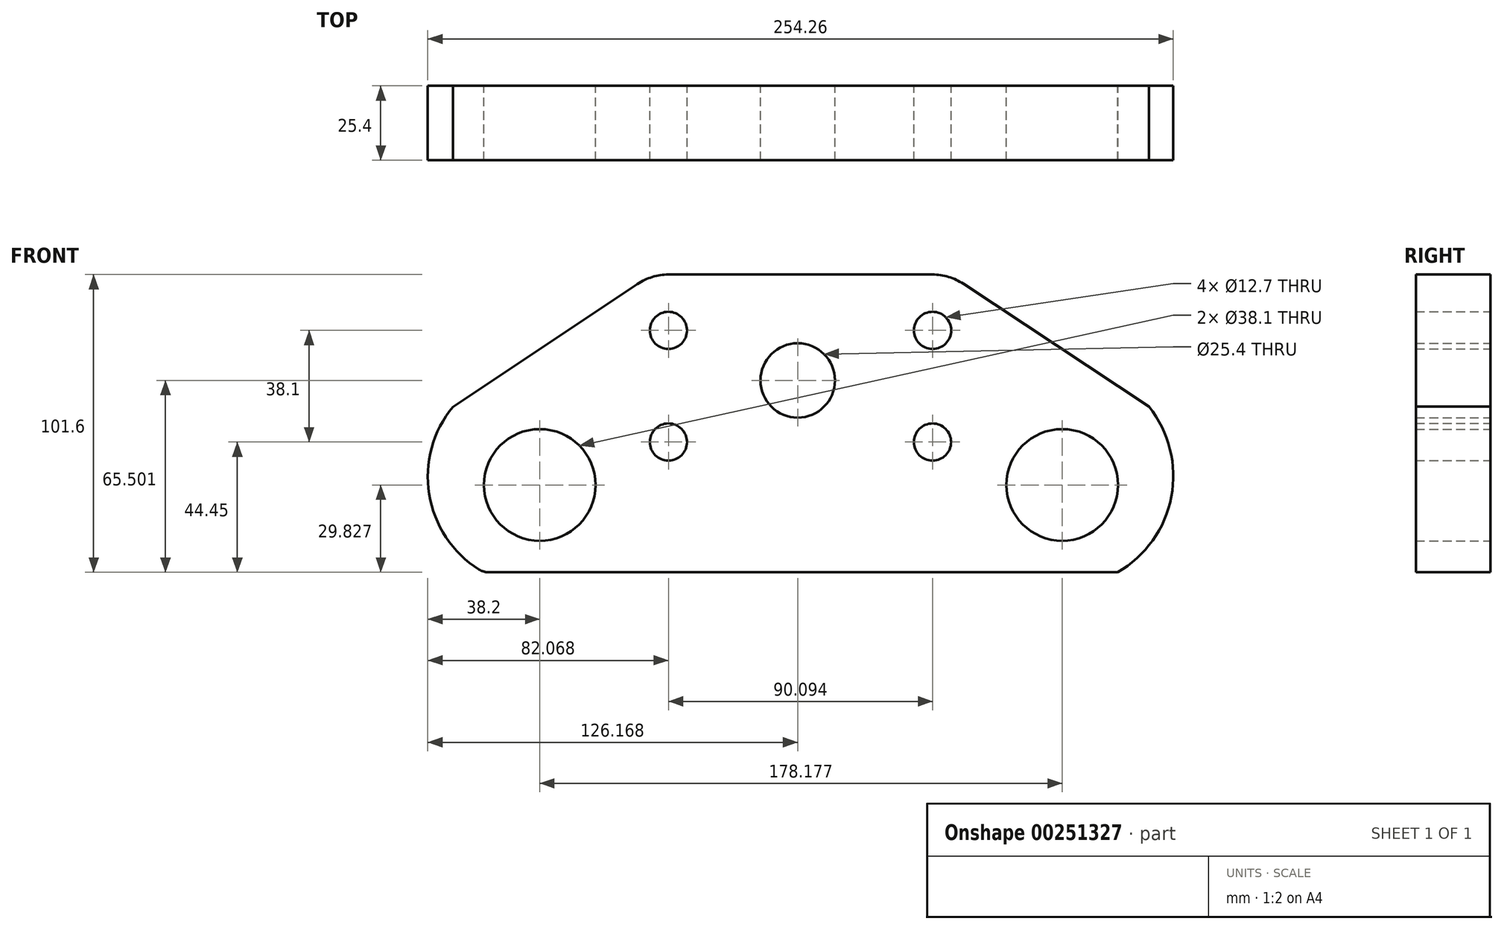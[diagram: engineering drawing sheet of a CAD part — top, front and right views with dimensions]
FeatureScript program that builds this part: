
annotation { "Feature Type Name" : "Feature", "Feature Type Description" : "" }
export const myFeature = defineFeature(function(context is Context, id is Id, definition is map)
    precondition{}
    {
        {
            var Q0;
            Q0=qCreatedBy(makeId("Front.planeOp"),FACE);
            var sketch = newSketch(context, id + "F0", { "sketchPlane" : qUnion([Q0])});
            skLineSegment(sketch, "E0", {"start": v(20.78, 0) * mm, "end": v(235.13, 0) * mm});
            skPoint(sketch, "E1", {"position": v(0, 0) * mm});
            skLineSegment(sketch, "E2", {"start": v(127, 101.6) * mm, "end": v(127, 0) * mm, "construction": true});
            skPoint(sketch, "E2.startSnap0", {"position": v(127, 0) * mm});
            skLineSegment(sketch, "E3", {"start": v(127, 101.6) * mm, "end": v(172.06, 101.6) * mm});
            skLineSegment(sketch, "E4", {"start": v(127, 101.6) * mm, "end": v(81.97, 101.6) * mm});
            skLineSegment(sketch, "E5", {"start": v(71.4, 98.4) * mm, "end": v(8.48, 56.46) * mm});
            skLineSegment(sketch, "E6", {"start": v(182.58, 98.43) * mm, "end": v(245.86, 56.51) * mm});
            skPoint(sketch, "E7.visualSharp", {"position": v(254.48, 50.8) * mm});
            skPoint(sketch, "E8.visualSharp", {"position": v(254, 0) * mm});
            skPoint(sketch, "E9.visualSharp", {"position": v(177.8, 101.6) * mm});
            skArc(sketch, "E9.filletArc", {"start": v(182.58, 98.43) * mm, "mid": v(177.56, 100.8) * mm, "end": v(172.06, 101.6) * mm});
            skPoint(sketch, "E10.visualSharp", {"position": v(76.2, 101.6) * mm});
            skArc(sketch, "E10.filletArc", {"start": v(81.97, 101.6) * mm, "mid": v(76.45, 100.78) * mm, "end": v(71.4, 98.4) * mm});
            skPoint(sketch, "E11.visualSharp", {"position": v(0, 50.8) * mm});
            skLineSegment(sketch, "E12", {"start": v(0, 29.83) * mm, "end": v(38.1, 29.83) * mm, "construction": true});
            skCircle(sketch, "E13", {"center": v(38.1, 29.83) * mm, "radius": 19.05 * mm});
            skLineSegment(sketch, "E14", {"start": v(254.39, 29.66) * mm, "end": v(216.29, 29.66) * mm, "construction": true});
            skPoint(sketch, "E14.startSnap0", {"position": v(254.28, 29.66) * mm});
            skCircle(sketch, "E15", {"center": v(216.28, 29.83) * mm, "radius": 19.05 * mm});
            skLineSegment(sketch, "E16", {"start": v(127, 101.6) * mm, "end": v(127, 63.5) * mm});
            skCircle(sketch, "E17", {"center": v(126.07, 65.5) * mm, "radius": 12.7 * mm});
            skLineSegment(sketch, "E18", {"start": v(81.97, 44.45) * mm, "end": v(81.97, 82.55) * mm});
            skLineSegment(sketch, "E19.MirrorCS", {"start": v(172.03, 44.45) * mm, "end": v(172.03, 82.55) * mm});
            skCircle(sketch, "E20", {"center": v(81.97, 82.55) * mm, "radius": 6.35 * mm});
            skCircle(sketch, "E21", {"center": v(81.97, 44.45) * mm, "radius": 6.35 * mm});
            skCircle(sketch, "E22", {"center": v(172.06, 82.55) * mm, "radius": 6.35 * mm});
            skCircle(sketch, "E23", {"center": v(172.03, 44.45) * mm, "radius": 6.35 * mm});
            skPoint(sketch, "E24.orphan", {"position": v(0, 19.05) * mm});
            skPoint(sketch, "E25.end.orphan", {"position": v(0, 40.6) * mm});
            skPoint(sketch, "E26.start.orphan", {"position": v(254.18, 18.87) * mm});
            skPoint(sketch, "E7.filletArc.start.orphan", {"position": v(254.39, 40.45) * mm});
            skArc(sketch, "E27", {"start": v(235.13, 0) * mm, "mid": v(253.5, 25.79) * mm, "end": v(245.86, 56.51) * mm});
            skArc(sketch, "E28", {"start": v(8.48, 56.46) * mm, "mid": v(0.37, 26.69) * mm, "end": v(17.41, 0.97) * mm});
            skPoint(sketch, "E29.visualSharp", {"position": v(19.05, 0) * mm});
            skArc(sketch, "E29.filletArc", {"start": v(17.41, 0.97) * mm, "mid": v(19.03, 0.25) * mm, "end": v(20.78, 0) * mm});
            skSolve(sketch);
        }
        {
            var Q0;
            Q0=makeQuery(id+"F0.imprint","IMPRINT",FACE,{"disambiguationData":[TD([[makeQuery(id+"F0.imprint","IMPRINT",EDGE,{"derivedFrom":sQuery(id+"F0.wireOp",EDGE,"E0")}),1.0]])]});
            extrude(context, id + "F1", {"entities" : qUnion([Q0]), "depth" : 25.4 * mm});
        }
    });
